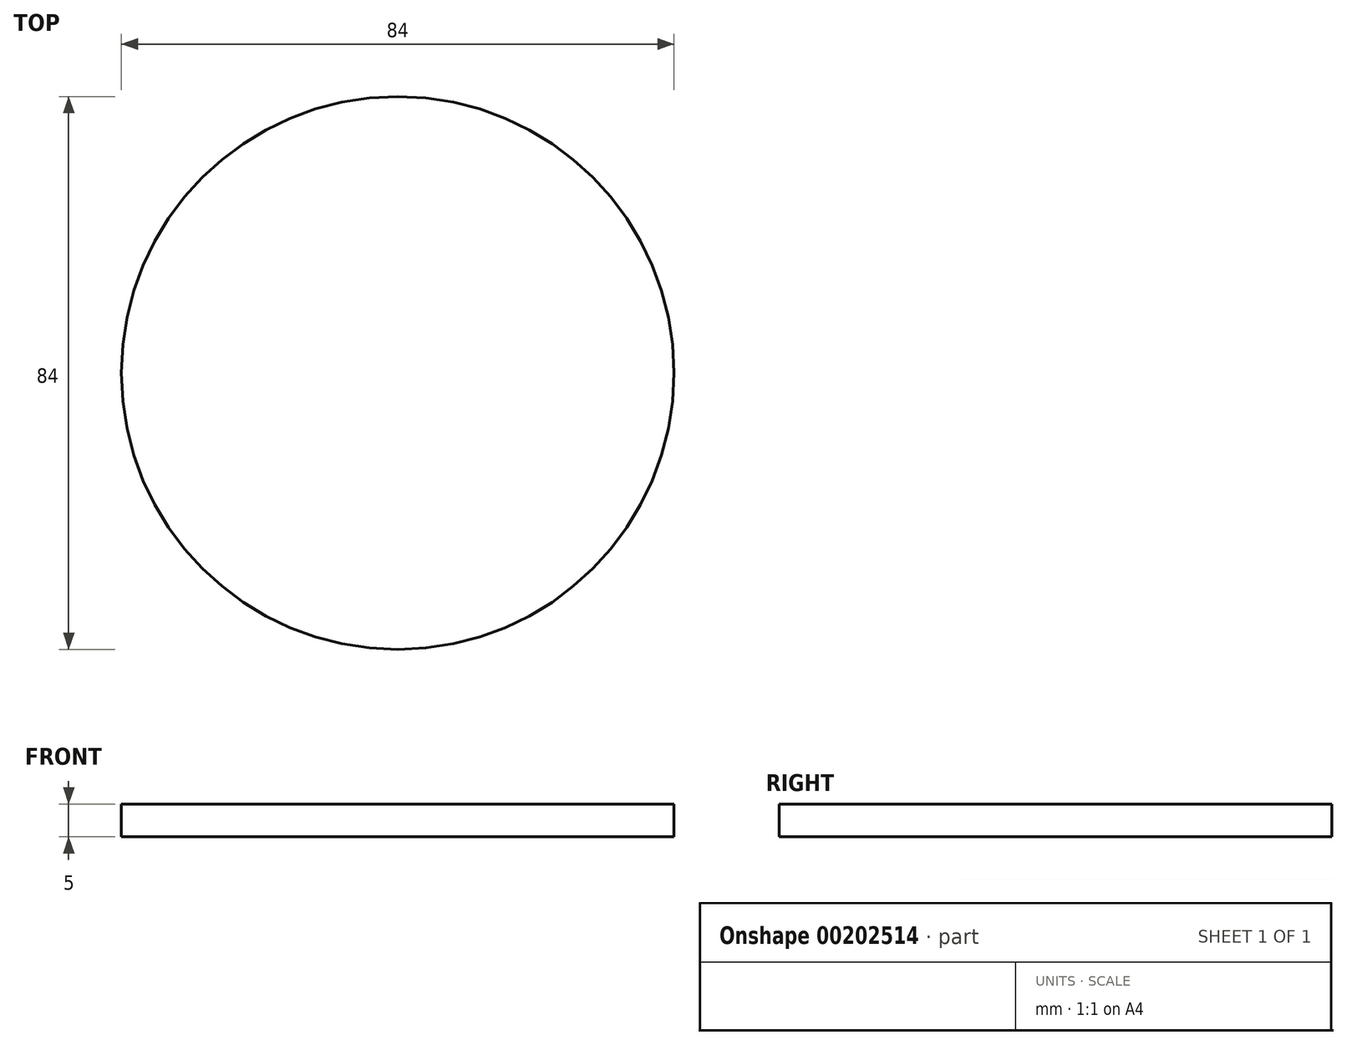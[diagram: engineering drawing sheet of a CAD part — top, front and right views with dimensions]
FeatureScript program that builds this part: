
annotation { "Feature Type Name" : "Feature", "Feature Type Description" : "" }
export const myFeature = defineFeature(function(context is Context, id is Id, definition is map)
    precondition{}
    {
        {
            var Q0;
            Q0=qCreatedBy(makeId("Top.planeOp"),FACE);
            var sketch = newSketch(context, id + "F0", { "sketchPlane" : qUnion([Q0])});
            skCircle(sketch, "E0", {"center": v(0, 0) * mm, "radius": 42 * mm});
            skSolve(sketch);
        }
        {
            var Q0;
            Q0 = qSketchRegion(id + "F0", true);
            extrude(context, id + "F1", {"entities" : qUnion([Q0]), "depth" : 5 * mm});
        }
    });
